# Revit family: SU-6000-G_GENERADO
name_source: partatom
category: Equipos mecánicos
revit_build: Autodesk Revit 2014 (Build: 20130308_1515(x64)
units: mm (PartAtom-declared; Revit-internal decimal feet)

## types (16) — shared parameters
Depth = 874 mm  [stored 2.86745 ft]
Fabricante = SAMMIC S.L.
Foodservice Equipment Identifier = Sí
Height = 1370 mm  [stored 4.49475 ft]
Revision Code = 1
URL = https://www.sammic.com
URL Cutsheet = http://www.sammic.com
Weight in Pounds = 793.7
Width = 1640 mm  [stored 5.38058 ft]

## per-type parameters (varying)
| type | Comentarios de tipo | Cycle | FL Amps | HP | Modelo | Specification by Manufacturer | Volts | Watts |
| Vacuum packing machine SU-6100G 400/50-60/3N | Double chamber vacuum packing machine. 100m³/h. | 50 Hz | 8 A | 5.36 | 1141032 | High performance model with tilting cover, double chamber and 4 x 662 mm. sealing bars.
100 m­³/h Busch vacuum pump.
Vacuum controlled by sensor. | 400 V | 4000 W |
| Vacuum packing machine SU-6100GP 400/50-60/3N | Double chamber vacuum packing machine. 100m³/h. | 50 Hz | 8 A | 5.36 | 1141036 | High performance model with tilting cover, double chamber and 4 x 662 mm. sealing bars.
100 m­³/h Busch vacuum pump.
Vacuum controlled by sensor. | 400 V | 4000 W |
| Vacuum packing machine SU-6100G+ 400/50-60/3N | Double chamber vacuum packing machine. 100m³/h. | 50 Hz | 8 A | 5.36 | 1141037 | High performance model with tilting cover, double chamber and 4 x 662 mm. sealing bars.
100 m­³/h Busch vacuum pump.
Vacuum controlled by sensor. | 400 V | 4000 W |
| Vacuum packing machine SU-6100GP+ 400/50-60/3N | Double chamber vacuum packing machine. 100m³/h. | 50 Hz | 8 A | 5.36 | 1141038 | High performance model with tilting cover, double chamber and 4 x 662 mm. sealing bars.
100 m­³/h Busch vacuum pump.
Vacuum controlled by sensor. | 400 V | 4000 W |
| Vacuum packing machine SU-6100G 220/60/3 | Double chamber vacuum packing machine. 100m³/h. | 60 Hz | 15 A | 6.97 | 1141042 | High performance model with tilting cover, double chamber and 4 x 662 mm. sealing bars.
100 m­³/h Busch vacuum pump.
Vacuum controlled by sensor. | 220 V | 5200 W |
| Vacuum packing machine SU-6100GP 220/60/3 | Double chamber vacuum packing machine. 100m³/h. | 60 Hz | 15 A | 6.97 | 1141046 | High performance model with tilting cover, double chamber and 4 x 662 mm. sealing bars.
100 m­³/h Busch vacuum pump.
Vacuum controlled by sensor. | 220 V | 5200 W |
| Vacuum packing machine SU-6100G+ 220/60/3 | Double chamber vacuum packing machine. 100m³/h. | 60 Hz | 15 A | 6.97 | 1141047 | High performance model with tilting cover, double chamber and 4 x 662 mm. sealing bars.
100 m­³/h Busch vacuum pump.
Vacuum controlled by sensor. | 220 V | 5200 W |
| Vacuum packing machine SU-6100GP+ 220/60/3 | Double chamber vacuum packing machine. 100m³/h. | 60 Hz | 15 A | 6.97 | 1141048 | High performance model with tilting cover, double chamber and 4 x 662 mm. sealing bars.
100 m­³/h Busch vacuum pump.
Vacuum controlled by sensor. | 220 V | 5200 W |
| Vacuum packing machine SU-6160G 400/50-60/3N | Double chamber vacuum packing machine. 160m³/h. | 50 Hz | 11 A | 8.05 | 1141052 | High performance model with tilting cover, double chamber and 4 x 662 mm. sealing bars.
160 m­³/h Busch vacuum pump.
Vacuum controlled by sensor. | 400 V | 6000 W |
| Vacuum packing machine SU-6160GP 400/50-60/3N | Double chamber vacuum packing machine. 160m³/h. | 50 Hz | 11 A | 8.05 | 1141056 | High performance model with tilting cover, double chamber and 4 x 662 mm. sealing bars.
160 m­³/h Busch vacuum pump.
Vacuum controlled by sensor. | 400 V | 6000 W |
| Vacuum packing machine SU-6160G+ 400/50-60/3N | Double chamber vacuum packing machine. 160m³/h. | 50 Hz | 11 A | 8.05 | 1141057 | High performance model with tilting cover, double chamber and 4 x 662 mm. sealing bars.
160 m­³/h Busch vacuum pump.
Vacuum controlled by sensor. | 400 V | 6000 W |
| Vacuum packing machine SU-6160GP+ 400/50-60/3N | Double chamber vacuum packing machine. 160m³/h. | 50 Hz | 11 A | 8.05 | 1141058 | High performance model with tilting cover, double chamber and 4 x 662 mm. sealing bars.
160 m­³/h Busch vacuum pump.
Vacuum controlled by sensor. | 400 V | 6000 W |
| Vacuum packing machine SU-6160G 220/60/3 | Double chamber vacuum packing machine. 160m³/h. | 60 Hz | 17 A | 8.05 | 1141062 | High performance model with tilting cover, double chamber and 4 x 662 mm. sealing bars.
160 m­³/h Busch vacuum pump.
Vacuum controlled by sensor. | 220 V | 6000 W |
| Vacuum packing machine SU-6160GP 220/60/3 | Double chamber vacuum packing machine. 160m³/h. | 60 Hz | 17 A | 8.05 | 1141066 | High performance model with tilting cover, double chamber and 4 x 662 mm. sealing bars.
160 m­³/h Busch vacuum pump.
Vacuum controlled by sensor. | 220 V | 6000 W |
| Vacuum packing machine SU-6160G+ 220/60/3 | Double chamber vacuum packing machine. 160m³/h. | 60 Hz | 17 A | 8.05 | 1141067 | High performance model with tilting cover, double chamber and 4 x 662 mm. sealing bars.
160 m­³/h Busch vacuum pump.
Vacuum controlled by sensor. | 220 V | 6000 W |
| Vacuum packing machine SU-6160GP+ 220/60/3 | Double chamber vacuum packing machine. 160m³/h. | 60 Hz | 17 A | 8.05 | 1141068 | High performance model with tilting cover, double chamber and 4 x 662 mm. sealing bars.
160 m­³/h Busch vacuum pump.
Vacuum controlled by sensor. | 220 V | 6000 W |

note: column(s) folded — value = type name in every type: Descripción

note: [stored X ft] marks values corroborated as IEEE doubles in the binary element streams (Revit-internal decimal feet)
